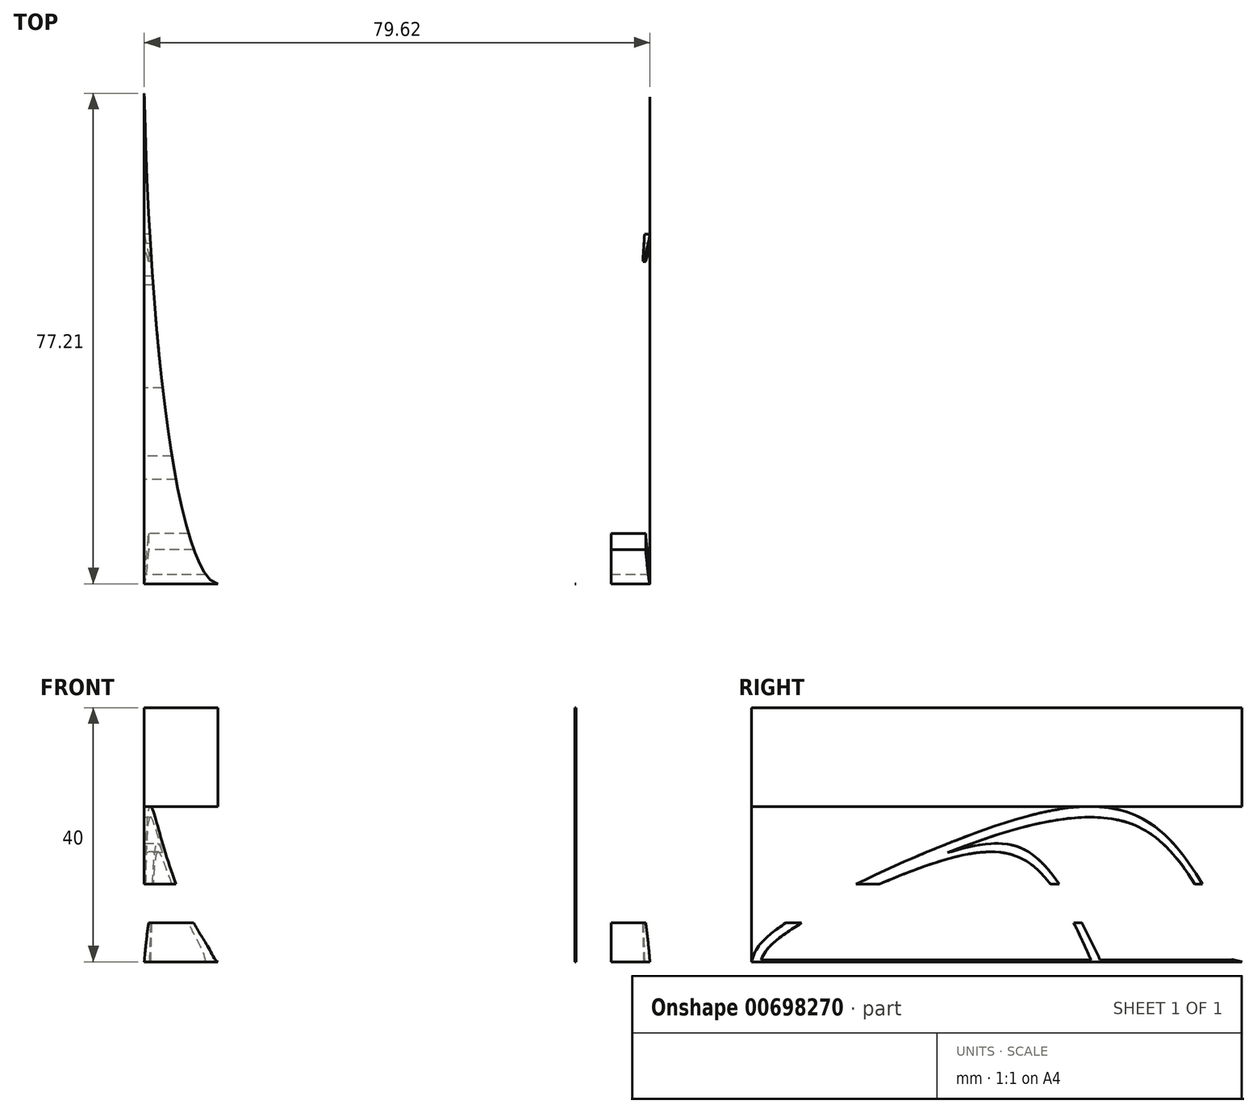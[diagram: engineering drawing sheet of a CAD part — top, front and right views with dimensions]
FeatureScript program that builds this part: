
annotation { "Feature Type Name" : "Feature", "Feature Type Description" : "" }
export const myFeature = defineFeature(function(context is Context, id is Id, definition is map)
    precondition{}
    {
        {
            var Q0;
            Q0=qCreatedBy(makeId("Top.planeOp"),FACE);
            var sketch = newSketch(context, id + "F0", { "sketchPlane" : qUnion([Q0])});
            skPoint(sketch, "E0", {"position": v(39.81, 38.84) * mm});
            skPoint(sketch, "E1", {"position": v(-39.81, 38.84) * mm});
            skPoint(sketch, "E2", {"position": v(-28, -38.37) * mm});
            skPoint(sketch, "E3", {"position": v(28, -38.37) * mm});
            skLineSegment(sketch, "E4", {"start": v(39.81, 38.84) * mm, "end": v(-39.81, 38.84) * mm});
            skLineSegment(sketch, "E5", {"start": v(28, -38.37) * mm, "end": v(-28, -38.37) * mm});
            skFitSpline(sketch, "E6.0", {"points": [v(28, -38.37) * mm, v(28.17, -38.37) * mm, v(28.4, -38.33) * mm, v(28.71, -38.2) * mm, v(29, -38.06) * mm, v(29.33, -37.8) * mm, v(29.67, -37.47) * mm, v(29.98, -37.1) * mm, v(30.36, -36.56) * mm, v(30.77, -35.86) * mm, v(31.2, -35) * mm, v(31.71, -33.82) * mm, v(32.27, -32.3) * mm, v(32.84, -30.46) * mm, v(33.35, -28.6) * mm, v(33.8, -26.73) * mm, v(34.35, -24.23) * mm, v(34.96, -21.09) * mm, v(35.6, -17.3) * mm, v(36.16, -13.5) * mm, v(36.65, -9.68) * mm, v(37.1, -5.85) * mm, v(37.5, -2.03) * mm, v(37.86, 1.8) * mm, v(38.29, 6.9) * mm, v(38.74, 13.27) * mm, v(39.18, 20.93) * mm, v(39.52, 28.6) * mm, v(39.76, 36.25) * mm, v(39.93, 43.92) * mm, v(40.03, 54.15) * mm, v(39.96, 66.93) * mm, v(39.69, 77.17) * mm, v(39.5, 82.3) * mm]});
            skFitSpline(sketch, "E7.0", {"points": [v(-39.81, 38.84) * mm, v(-39.74, 35.53) * mm, v(-39.54, 28.9) * mm, v(-39.16, 20.6) * mm, v(-38.78, 13.98) * mm, v(-38.44, 9.02) * mm, v(-38.06, 4.06) * mm, v(-37.61, -0.88) * mm, v(-37.1, -5.82) * mm, v(-36.52, -10.75) * mm, v(-35.96, -14.85) * mm, v(-35.46, -18.12) * mm, v(-35.05, -20.56) * mm, v(-34.6, -23) * mm, v(-34.1, -25.44) * mm, v(-33.53, -27.87) * mm, v(-33, -29.88) * mm, v(-32.52, -31.48) * mm, v(-32.13, -32.68) * mm, v(-31.69, -33.87) * mm, v(-31.28, -34.83) * mm, v(-30.9, -35.6) * mm, v(-30.6, -36.15) * mm, v(-30.27, -36.69) * mm, v(-29.9, -37.2) * mm, v(-29.48, -37.68) * mm, v(-28.99, -38.08) * mm, v(-28.5, -38.31) * mm, v(-28.08, -38.38) * mm, v(-27.87, -38.37) * mm, v(-27.77, -38.35) * mm]});
            skLineSegment(sketch, "E8.bottom", {"start": v(-39.81, 38.84) * mm, "end": v(39.81, 38.84) * mm});
            skLineSegment(sketch, "E8.top", {"start": v(-39.81, -38.37) * mm, "end": v(39.81, -38.37) * mm});
            skLineSegment(sketch, "E8.left", {"start": v(-39.81, 38.84) * mm, "end": v(-39.81, -38.37) * mm});
            skLineSegment(sketch, "E8.right", {"start": v(39.81, 38.84) * mm, "end": v(39.81, -38.37) * mm});
            skSolve(sketch);
        }
        {
            var Q0;
            {var subQ0=sQuery(id+"F0.wireOp",EDGE,"E6.0");Q0=makeQuery(id+"F0.imprint","IMPRINT",FACE,{"disambiguationData":[TD([[makeQuery(id+"F0.imprint","IMPRINT",EDGE,{"derivedFrom":subQ0}),-1.0]])]});}
            var Q1;
            {var subQ1=sQuery(id+"F0.wireOp",EDGE,"E6.0");Q1=makeQuery(id+"F0.imprint","IMPRINT",FACE,{"disambiguationData":[TD([[makeQuery(id+"F0.imprint","IMPRINT",EDGE,{"derivedFrom":subQ1}),1.0]])]});}
            var Q2;
            {var subQ0=sQuery(id+"F0.wireOp",EDGE,"E7.0");Q2=makeQuery(id+"F0.imprint","IMPRINT",FACE,{"disambiguationData":[TD([[makeQuery(id+"F0.imprint","IMPRINT",EDGE,{"derivedFrom":subQ0}),-1.0]])]});}
            extrude(context, id + "F1", {"entities" : qUnion([Q0, Q1, Q2]), "depth" : 40 * mm, "offsetDistance" : 25 * mm});
        }
        {
            var Q0;
            Q0=makeQuery(id+"F1.opExtrude","SWEPT_FACE",FACE,{"disambiguationData":[OSD([sQuery(id+"F0.wireOp",EDGE,"E8.left")])]});
            var sketch = newSketch(context, id + "F2", { "sketchPlane" : qUnion([Q0])});
            skFitSpline(sketch, "E9", {"points": [v(38.37, 0) * mm, v(36.2, 3.66) * mm, v(4, 19.95) * mm, v(-23.03, 22.6) * mm, v(-38.84, 0) * mm], "startDerivative": vector(-8.4, 29.66) * mm, "endDerivative": vector(-47.28, -100.41) * mm});
            skFitSpline(sketch, "E10", {"points": [v(-37.4, 0) * mm, v(-32.94, 9.49) * mm, v(-22.46, 21.28) * mm, v(4, 18.51) * mm, v(34.92, 3) * mm, v(36.93, 0) * mm], "startDerivative": vector(24.06, 55.07) * mm, "endDerivative": vector(8.6, -27.87) * mm});
            skFitSpline(sketch, "E11", {"points": [v(7.54, 17.17) * mm, v(-4.5, 17.7) * mm, v(-16.65, 0) * mm], "startDerivative": vector(-29.57, 8.19) * mm, "endDerivative": vector(-19.28, -40.17) * mm});
            skFitSpline(sketch, "E12", {"points": [v(-15.2, 0) * mm, v(-11.54, 7.65) * mm, v(-3.89, 16.4) * mm, v(8.95, 15.76) * mm, v(23.48, 10) * mm], "startDerivative": vector(15.52, 34.53) * mm, "endDerivative": vector(48.48, -20.3) * mm});
            skLineSegment(sketch, "E13", {"start": v(-38.84, 24.44) * mm, "end": v(38.37, 24.44) * mm});
            skLineSegment(sketch, "E14", {"start": v(38.06, 24.44) * mm, "end": v(-38.84, 24.44) * mm});
            skLineSegment(sketch, "E15", {"start": v(-38.84, 24.44) * mm, "end": v(-38.84, 0) * mm});
            skFitSpline(sketch, "E16", {"points": [v(38.37, 0) * mm, v(36.2, 3.66) * mm, v(4, 19.95) * mm, v(-23.03, 22.6) * mm, v(-38.84, 0) * mm], "startDerivative": vector(-8.4, 29.66) * mm, "endDerivative": vector(-47.28, -100.41) * mm});
            skLineSegment(sketch, "E17.top", {"start": v(38.06, 40) * mm, "end": v(38.37, 40) * mm});
            skLineSegment(sketch, "E17.right", {"start": v(38.37, 1.1) * mm, "end": v(38.37, 40) * mm});
            skSolve(sketch);
        }
        {
            var Q0;
            Q0=makeQuery(id+"F1.opExtrude","SWEPT_FACE",FACE,{"disambiguationData":[OSD([sQuery(id+"F0.wireOp",EDGE,"E8.top")])]});
            var sketch = newSketch(context, id + "F3", { "sketchPlane" : qUnion([Q0])});
            skPoint(sketch, "E18", {"position": v(-39.81, 24.44) * mm});
            skLineSegment(sketch, "E19", {"start": v(-39.81, 24.44) * mm, "end": v(39.81, 24.44) * mm});
            skLineSegment(sketch, "E20", {"start": v(-39.81, 24.44) * mm, "end": v(-39.81, 0) * mm});
            skPoint(sketch, "E21", {"position": v(-39.81, 12.22) * mm});
            skLineSegment(sketch, "E22", {"start": v(-39.81, 12.22) * mm, "end": v(-39.81, 0) * mm});
            skLineSegment(sketch, "E23", {"start": v(-39.81, 24.44) * mm, "end": v(-39.81, 12.22) * mm});
            skPoint(sketch, "E24", {"position": v(-39.81, 18.33) * mm});
            skPoint(sketch, "E25", {"position": v(-39.81, 6.11) * mm});
            skLineSegment(sketch, "E26", {"start": v(-39.81, 18.33) * mm, "end": v(39.81, 18.33) * mm});
            skLineSegment(sketch, "E27", {"start": v(39.81, 18.33) * mm, "end": v(39.81, 6.11) * mm});
            skLineSegment(sketch, "E28", {"start": v(39.81, 6.11) * mm, "end": v(-39.81, 6.11) * mm});
            skLineSegment(sketch, "E29", {"start": v(-39.81, 12.22) * mm, "end": v(39.81, 12.22) * mm});
            skPoint(sketch, "E30", {"position": v(-33.7, 0) * mm});
            skPoint(sketch, "E31", {"position": v(33.7, 0) * mm});
            skLineSegment(sketch, "E32", {"start": v(-33.7, 0) * mm, "end": v(-33.7, 24.44) * mm});
            skLineSegment(sketch, "E33", {"start": v(-33.7, 24.44) * mm, "end": v(33.7, 24.44) * mm});
            skLineSegment(sketch, "E34", {"start": v(33.7, 24.44) * mm, "end": v(33.7, 0) * mm});
            skFitSpline(sketch, "E35", {"points": [v(-39.81, 0) * mm, v(-33.7, 18.33) * mm, v(0, 24.44) * mm, v(33.7, 18.33) * mm, v(39.81, 0) * mm], "startDerivative": vector(9.29, 98.82) * mm, "endDerivative": vector(9.29, -98.82) * mm});
            skPoint(sketch, "E36", {"position": v(-3, 24.43) * mm});
            skPoint(sketch, "E37", {"position": v(3, 24.43) * mm});
            skPoint(sketch, "E38", {"position": v(36.81, 0) * mm});
            skPoint(sketch, "E39", {"position": v(-36.81, 0) * mm});
            skPoint(sketch, "E40", {"position": v(-34.68, 12.22) * mm});
            skPoint(sketch, "E41", {"position": v(-30.7, 18.33) * mm});
            skPoint(sketch, "E42", {"position": v(-36.13, 6.11) * mm});
            skPoint(sketch, "E43", {"position": v(-3, 21.43) * mm});
            skPoint(sketch, "E44", {"position": v(3, 21.43) * mm});
            skPoint(sketch, "E45", {"position": v(30.7, 18.33) * mm});
            skPoint(sketch, "E46", {"position": v(34.69, 12.22) * mm});
            skPoint(sketch, "E47", {"position": v(36.13, 6.11) * mm});
            skPoint(sketch, "E48", {"position": v(-39.13, 6.11) * mm});
            skPoint(sketch, "E49", {"position": v(-37.68, 12.22) * mm});
            skLineSegment(sketch, "E50", {"start": v(-3, 24.43) * mm, "end": v(-3, 0) * mm});
            skLineSegment(sketch, "E51", {"start": v(3, 24.43) * mm, "end": v(3, 0) * mm});
            skPoint(sketch, "E52", {"position": v(39.13, 6.11) * mm});
            skPoint(sketch, "E53", {"position": v(37.69, 12.22) * mm});
            skFitSpline(sketch, "E54", {"points": [v(-36.81, 0) * mm, v(-36.13, 6.1) * mm, v(-34.68, 12.22) * mm, v(-30.7, 18.33) * mm, v(-3, 21.43) * mm, v(3, 21.43) * mm, v(30.7, 18.33) * mm, v(34.69, 12.22) * mm, v(36.13, 6.1) * mm, v(36.81, 0) * mm], "startDerivative": vector(5.43, 70.33) * mm, "endDerivative": vector(5.43, -70.33) * mm});
            skSolve(sketch);
        }
        {
            var Q0;
            {var subQ0=sQuery(id+"F3.wireOp",EDGE,"E23");var subQ5=sQuery(id+"F3.wireOp",EDGE,"E26");var subQ6=makeQuery(id+"F3.imprint","INTERSECT",VERTEX,{"derivedFrom":[subQ0,subQ5]});Q0=makeQuery(id+"F3.imprint","IMPRINT",FACE,{"disambiguationData":[TD([[makeQuery(id+"F3.imprint","IMPRINT",EDGE,{"disambiguationData":[TD([[subQ6,-1.0]])],"derivedFrom":subQ5}),1.0]])]});}
            var Q1;
            {var subQ1=sQuery(id+"F3.wireOp",EDGE,"E23");var subQ3=sQuery(id+"F3.wireOp",EDGE,"E26");var subQ4=makeQuery(id+"F3.imprint","INTERSECT",VERTEX,{"derivedFrom":[subQ1,subQ3]});Q1=makeQuery(id+"F3.imprint","IMPRINT",FACE,{"disambiguationData":[TD([[makeQuery(id+"F3.imprint","IMPRINT",EDGE,{"disambiguationData":[TD([[subQ4,-1.0]])],"derivedFrom":subQ1}),1.0]])]});}
            var Q2;
            {var subQ1=sQuery(id+"F3.wireOp",EDGE,"E22");var subQ3=sQuery(id+"F3.wireOp",EDGE,"E28");var subQ4=makeQuery(id+"F3.imprint","INTERSECT",VERTEX,{"derivedFrom":[subQ1,subQ3]});Q2=makeQuery(id+"F3.imprint","IMPRINT",FACE,{"disambiguationData":[TD([[makeQuery(id+"F3.imprint","IMPRINT",EDGE,{"disambiguationData":[TD([[subQ4,1.0]])],"derivedFrom":subQ3}),-1.0]])]});}
            var Q3;
            {var subQ1=sQuery(id+"F3.wireOp",EDGE,"E22");var subQ3=sQuery(id+"F3.wireOp",EDGE,"E28");var subQ4=makeQuery(id+"F3.imprint","INTERSECT",VERTEX,{"derivedFrom":[subQ1,subQ3]});Q3=makeQuery(id+"F3.imprint","IMPRINT",FACE,{"disambiguationData":[TD([[makeQuery(id+"F3.imprint","IMPRINT",EDGE,{"disambiguationData":[TD([[subQ4,1.0]])],"derivedFrom":subQ3}),1.0]])]});}
            var Q4;
            {var subQ0=sQuery(id+"F3.wireOp",EDGE,"E28");var subQ4=sQuery(id+"F3.wireOp",EDGE,"E35");var subQ5=makeQuery(id+"F3.imprint","INTERSECT",VERTEX,{"disambiguationData":[OD(0.0)],"derivedFrom":[subQ0,subQ4]});Q4=makeQuery(id+"F3.imprint","IMPRINT",FACE,{"disambiguationData":[TD([[makeQuery(id+"F3.imprint","IMPRINT",EDGE,{"disambiguationData":[TD([[subQ5,1.0]])],"derivedFrom":subQ0}),1.0]])]});}
            var Q5;
            {var subQ1=sQuery(id+"F3.wireOp",EDGE,"E27");var subQ3=sQuery(id+"F3.wireOp",EDGE,"E29");var subQ4=makeQuery(id+"F3.imprint","INTERSECT",VERTEX,{"derivedFrom":[subQ1,subQ3]});Q5=makeQuery(id+"F3.imprint","IMPRINT",FACE,{"disambiguationData":[TD([[makeQuery(id+"F3.imprint","IMPRINT",EDGE,{"disambiguationData":[TD([[subQ4,1.0]])],"derivedFrom":subQ3}),-1.0]])]});}
            var Q6;
            {var subQ0=sQuery(id+"F3.wireOp",EDGE,"E27");var subQ5=sQuery(id+"F3.wireOp",EDGE,"E29");var subQ6=makeQuery(id+"F3.imprint","INTERSECT",VERTEX,{"derivedFrom":[subQ0,subQ5]});Q6=makeQuery(id+"F3.imprint","IMPRINT",FACE,{"disambiguationData":[TD([[makeQuery(id+"F3.imprint","IMPRINT",EDGE,{"disambiguationData":[TD([[subQ6,1.0]])],"derivedFrom":subQ5}),1.0]])]});}
            var Q7;
            {var subQ0=sQuery(id+"F3.wireOp",EDGE,"E19");var subQ1=makeQuery(id+"F1.opExtrude","SWEPT_EDGE",EDGE,{"disambiguationData":[OSD([sQuery(id+"F0.wireOp",EDGE,"E8.top"),sQuery(id+"F0.wireOp",EDGE,"E8.right")])]});var subQ2=makeQuery(id+"F3.imprint","INTERSECT",VERTEX,{"derivedFrom":[subQ1,subQ0]});Q7=makeQuery(id+"F3.imprint","IMPRINT",FACE,{"disambiguationData":[TD([[makeQuery(id+"F3.imprint","IMPRINT",EDGE,{"disambiguationData":[TD([[subQ2,1.0]])],"derivedFrom":subQ0}),-1.0]])]});}
            var Q8;
            {var subQ1=sQuery(id+"F3.wireOp",EDGE,"E33");var subQ3=sQuery(id+"F3.wireOp",EDGE,"E35");var subQ4=makeQuery(id+"F3.imprint","INTERSECT",VERTEX,{"derivedFrom":[subQ1,subQ3]});Q8=makeQuery(id+"F3.imprint","IMPRINT",FACE,{"disambiguationData":[TD([[makeQuery(id+"F3.imprint","IMPRINT",EDGE,{"disambiguationData":[TD([[subQ4,-1.0]])],"derivedFrom":subQ1}),-1.0]])]});}
            var Q9;
            {var subQ0=sQuery(id+"F3.wireOp",EDGE,"E33");var subQ3=sQuery(id+"F3.wireOp",EDGE,"E35");var subQ5=makeQuery(id+"F3.imprint","INTERSECT",VERTEX,{"derivedFrom":[subQ0,subQ3]});Q9=makeQuery(id+"F3.imprint","IMPRINT",FACE,{"disambiguationData":[TD([[makeQuery(id+"F3.imprint","IMPRINT",EDGE,{"disambiguationData":[TD([[subQ5,1.0]])],"derivedFrom":subQ0}),-1.0]])]});}
            var Q10;
            {var subQ4=sQuery(id+"F0.wireOp",EDGE,"E8.top");var subQ10=makeQuery(id+"F1.opExtrude","CAP_EDGE",EDGE,{"disambiguationData":[OSD([subQ4])],"isStart":false});Q10=makeQuery(id+"F3.imprint","IMPRINT",FACE,{"disambiguationData":[TD([[makeQuery(id+"F3.imprint","IMPRINT",EDGE,{"derivedFrom":subQ10}),-1.0]])]});}
            extrude(context, id + "F4", {"entities" : qUnion([Q0, Q1, Q2, Q3, Q4, Q5, Q6, Q7, Q8, Q9, Q10]), "operationType" : NewBodyOperationType.REMOVE, "oppositeDirection" : true, "depth" : 88.6 * mm, "offsetDistance" : 25 * mm});
        }
        {
            var Q0;
            {var subQ0=sQuery(id+"F3.wireOp",EDGE,"E54");var subQ1=sQuery(id+"F3.wireOp",EDGE,"E26");var subQ2=makeQuery(id+"F3.imprint","INTERSECT",VERTEX,{"disambiguationData":[OD(0.0)],"derivedFrom":[subQ1,subQ0]});Q0=makeQuery(id+"F3.imprint","IMPRINT",FACE,{"disambiguationData":[TD([[makeQuery(id+"F3.imprint","IMPRINT",EDGE,{"disambiguationData":[TD([[subQ2,-1.0]])],"derivedFrom":subQ1}),1.0]])]});}
            var Q1;
            {var subQ3=sQuery(id+"F3.wireOp",EDGE,"E54");var subQ6=sQuery(id+"F3.wireOp",EDGE,"E26");var subQ9=makeQuery(id+"F3.imprint","INTERSECT",VERTEX,{"disambiguationData":[OD(0.0)],"derivedFrom":[subQ6,subQ3]});Q1=makeQuery(id+"F3.imprint","IMPRINT",FACE,{"disambiguationData":[TD([[makeQuery(id+"F3.imprint","IMPRINT",EDGE,{"disambiguationData":[TD([[subQ9,-1.0]])],"derivedFrom":subQ6}),-1.0]])]});}
            var Q2;
            {var subQ0=sQuery(id+"F3.wireOp",EDGE,"E50");var subQ1=sQuery(id+"F3.wireOp",EDGE,"E28");var subQ2=makeQuery(id+"F3.imprint","INTERSECT",VERTEX,{"derivedFrom":[subQ1,subQ0]});Q2=makeQuery(id+"F3.imprint","IMPRINT",FACE,{"disambiguationData":[TD([[makeQuery(id+"F3.imprint","IMPRINT",EDGE,{"disambiguationData":[TD([[subQ2,-1.0]])],"derivedFrom":subQ1}),-1.0]])]});}
            var Q3;
            {var subQ0=sQuery(id+"F3.wireOp",EDGE,"E54");var subQ1=sQuery(id+"F3.wireOp",EDGE,"E29");var subQ2=makeQuery(id+"F3.imprint","INTERSECT",VERTEX,{"disambiguationData":[OD(0.0)],"derivedFrom":[subQ1,subQ0]});Q3=makeQuery(id+"F3.imprint","IMPRINT",FACE,{"disambiguationData":[TD([[makeQuery(id+"F3.imprint","IMPRINT",EDGE,{"disambiguationData":[TD([[subQ2,-1.0]])],"derivedFrom":subQ1}),1.0]])]});}
            var Q4;
            {var subQ0=sQuery(id+"F3.wireOp",EDGE,"E32");var subQ1=sQuery(id+"F3.wireOp",EDGE,"E28");var subQ2=makeQuery(id+"F3.imprint","INTERSECT",VERTEX,{"derivedFrom":[subQ1,subQ0]});Q4=makeQuery(id+"F3.imprint","IMPRINT",FACE,{"disambiguationData":[TD([[makeQuery(id+"F3.imprint","IMPRINT",EDGE,{"disambiguationData":[TD([[subQ2,-1.0]])],"derivedFrom":subQ1}),-1.0]])]});}
            var Q5;
            {var subQ0=sQuery(id+"F3.wireOp",EDGE,"E32");var subQ1=sQuery(id+"F3.wireOp",EDGE,"E28");var subQ2=makeQuery(id+"F3.imprint","INTERSECT",VERTEX,{"derivedFrom":[subQ1,subQ0]});Q5=makeQuery(id+"F3.imprint","IMPRINT",FACE,{"disambiguationData":[TD([[makeQuery(id+"F3.imprint","IMPRINT",EDGE,{"disambiguationData":[TD([[subQ2,-1.0]])],"derivedFrom":subQ1}),1.0]])]});}
            var Q6;
            {var subQ0=sQuery(id+"F3.wireOp",EDGE,"E50");var subQ1=sQuery(id+"F3.wireOp",EDGE,"E28");var subQ2=makeQuery(id+"F3.imprint","INTERSECT",VERTEX,{"derivedFrom":[subQ1,subQ0]});Q6=makeQuery(id+"F3.imprint","IMPRINT",FACE,{"disambiguationData":[TD([[makeQuery(id+"F3.imprint","IMPRINT",EDGE,{"disambiguationData":[TD([[subQ2,-1.0]])],"derivedFrom":subQ1}),1.0]])]});}
            var Q7;
            {var subQ0=sQuery(id+"F3.wireOp",EDGE,"E34");var subQ1=sQuery(id+"F3.wireOp",EDGE,"E28");var subQ2=makeQuery(id+"F3.imprint","INTERSECT",VERTEX,{"derivedFrom":[subQ1,subQ0]});Q7=makeQuery(id+"F3.imprint","IMPRINT",FACE,{"disambiguationData":[TD([[makeQuery(id+"F3.imprint","IMPRINT",EDGE,{"disambiguationData":[TD([[subQ2,-1.0]])],"derivedFrom":subQ1}),-1.0]])]});}
            var Q8;
            {var subQ0=sQuery(id+"F3.wireOp",EDGE,"E34");var subQ1=sQuery(id+"F3.wireOp",EDGE,"E28");var subQ2=makeQuery(id+"F3.imprint","INTERSECT",VERTEX,{"derivedFrom":[subQ1,subQ0]});Q8=makeQuery(id+"F3.imprint","IMPRINT",FACE,{"disambiguationData":[TD([[makeQuery(id+"F3.imprint","IMPRINT",EDGE,{"disambiguationData":[TD([[subQ2,-1.0]])],"derivedFrom":subQ1}),1.0]])]});}
            var Q9;
            {var subQ0=sQuery(id+"F3.wireOp",EDGE,"E51");var subQ1=sQuery(id+"F3.wireOp",EDGE,"E28");var subQ2=makeQuery(id+"F3.imprint","INTERSECT",VERTEX,{"derivedFrom":[subQ1,subQ0]});Q9=makeQuery(id+"F3.imprint","IMPRINT",FACE,{"disambiguationData":[TD([[makeQuery(id+"F3.imprint","IMPRINT",EDGE,{"disambiguationData":[TD([[subQ2,-1.0]])],"derivedFrom":subQ1}),1.0]])]});}
            var Q10;
            {var subQ0=sQuery(id+"F3.wireOp",EDGE,"E51");var subQ1=sQuery(id+"F3.wireOp",EDGE,"E28");var subQ2=makeQuery(id+"F3.imprint","INTERSECT",VERTEX,{"derivedFrom":[subQ1,subQ0]});Q10=makeQuery(id+"F3.imprint","IMPRINT",FACE,{"disambiguationData":[TD([[makeQuery(id+"F3.imprint","IMPRINT",EDGE,{"disambiguationData":[TD([[subQ2,-1.0]])],"derivedFrom":subQ1}),-1.0]])]});}
            var Q11;
            {var subQ0=sQuery(id+"F3.wireOp",EDGE,"E50");var subQ1=sQuery(id+"F3.wireOp",EDGE,"E26");var subQ2=makeQuery(id+"F3.imprint","INTERSECT",VERTEX,{"derivedFrom":[subQ1,subQ0]});Q11=makeQuery(id+"F3.imprint","IMPRINT",FACE,{"disambiguationData":[TD([[makeQuery(id+"F3.imprint","IMPRINT",EDGE,{"disambiguationData":[TD([[subQ2,-1.0]])],"derivedFrom":subQ1}),-1.0]])]});}
            var Q12;
            {var subQ0=sQuery(id+"F3.wireOp",EDGE,"E50");var subQ1=sQuery(id+"F3.wireOp",EDGE,"E26");var subQ2=makeQuery(id+"F3.imprint","INTERSECT",VERTEX,{"derivedFrom":[subQ1,subQ0]});Q12=makeQuery(id+"F3.imprint","IMPRINT",FACE,{"disambiguationData":[TD([[makeQuery(id+"F3.imprint","IMPRINT",EDGE,{"disambiguationData":[TD([[subQ2,-1.0]])],"derivedFrom":subQ1}),1.0]])]});}
            var Q13;
            {var subQ0=sQuery(id+"F3.wireOp",EDGE,"E51");var subQ1=sQuery(id+"F3.wireOp",EDGE,"E26");var subQ2=makeQuery(id+"F3.imprint","INTERSECT",VERTEX,{"derivedFrom":[subQ1,subQ0]});Q13=makeQuery(id+"F3.imprint","IMPRINT",FACE,{"disambiguationData":[TD([[makeQuery(id+"F3.imprint","IMPRINT",EDGE,{"disambiguationData":[TD([[subQ2,-1.0]])],"derivedFrom":subQ1}),1.0]])]});}
            var Q14;
            {var subQ0=sQuery(id+"F3.wireOp",EDGE,"E51");var subQ1=sQuery(id+"F3.wireOp",EDGE,"E26");var subQ2=makeQuery(id+"F3.imprint","INTERSECT",VERTEX,{"derivedFrom":[subQ1,subQ0]});Q14=makeQuery(id+"F3.imprint","IMPRINT",FACE,{"disambiguationData":[TD([[makeQuery(id+"F3.imprint","IMPRINT",EDGE,{"disambiguationData":[TD([[subQ2,-1.0]])],"derivedFrom":subQ1}),-1.0]])]});}
            var Q15;
            {var subQ0=sQuery(id+"F3.wireOp",EDGE,"E54");var subQ1=sQuery(id+"F3.wireOp",EDGE,"E28");var subQ2=makeQuery(id+"F3.imprint","INTERSECT",VERTEX,{"disambiguationData":[OD(0.0)],"derivedFrom":[subQ1,subQ0]});Q15=makeQuery(id+"F3.imprint","IMPRINT",FACE,{"disambiguationData":[TD([[makeQuery(id+"F3.imprint","IMPRINT",EDGE,{"disambiguationData":[TD([[subQ2,-1.0]])],"derivedFrom":subQ1}),-1.0]])]});}
            var Q16;
            {var subQ0=sQuery(id+"F3.wireOp",EDGE,"E34");var subQ1=sQuery(id+"F3.wireOp",EDGE,"E29");var subQ2=makeQuery(id+"F3.imprint","INTERSECT",VERTEX,{"derivedFrom":[subQ1,subQ0]});Q16=makeQuery(id+"F3.imprint","IMPRINT",FACE,{"disambiguationData":[TD([[makeQuery(id+"F3.imprint","IMPRINT",EDGE,{"disambiguationData":[TD([[subQ2,-1.0]])],"derivedFrom":subQ1}),1.0]])]});}
            var Q17;
            {var subQ0=sQuery(id+"F3.wireOp",EDGE,"E54");var subQ1=sQuery(id+"F3.wireOp",EDGE,"E28");var subQ2=makeQuery(id+"F3.imprint","INTERSECT",VERTEX,{"disambiguationData":[OD(0.0)],"derivedFrom":[subQ1,subQ0]});Q17=makeQuery(id+"F3.imprint","IMPRINT",FACE,{"disambiguationData":[TD([[makeQuery(id+"F3.imprint","IMPRINT",EDGE,{"disambiguationData":[TD([[subQ2,-1.0]])],"derivedFrom":subQ1}),1.0]])]});}
            extrude(context, id + "F5", {"entities" : qUnion([Q0, Q1, Q2, Q3, Q4, Q5, Q6, Q7, Q8, Q9, Q10, Q11, Q12, Q13, Q14, Q15, Q16, Q17]), "operationType" : NewBodyOperationType.REMOVE, "oppositeDirection" : true, "depth" : 97.6 * mm, "offsetDistance" : 25 * mm});
        }
        {
            var Q0;
            {var subQ0=sQuery(id+"F2.wireOp",EDGE,"E15");Q0=makeQuery(id+"F2.imprint","IMPRINT",FACE,{"disambiguationData":[TD([[makeQuery(id+"F2.imprint","IMPRINT",EDGE,{"derivedFrom":subQ0}),1.0]])]});}
            var Q1;
            {var subQ3=sQuery(id+"F2.wireOp",EDGE,"E11");Q1=makeQuery(id+"F2.imprint","IMPRINT",FACE,{"disambiguationData":[TD([[makeQuery(id+"F2.imprint","IMPRINT",EDGE,{"derivedFrom":subQ3}),-1.0]])]});}
            var Q2;
            {var subQ1=sQuery(id+"F2.wireOp",EDGE,"E13");Q2=makeQuery(id+"F2.imprint","IMPRINT",FACE,{"disambiguationData":[TD([[makeQuery(id+"F2.imprint","IMPRINT",EDGE,{"derivedFrom":subQ1}),-1.0]])]});}
            var Q3;
            {var subQ3=sQuery(id+"F2.wireOp",EDGE,"E12");Q3=makeQuery(id+"F2.imprint","IMPRINT",FACE,{"disambiguationData":[TD([[makeQuery(id+"F2.imprint","IMPRINT",EDGE,{"derivedFrom":subQ3}),-1.0]])]});}
            extrude(context, id + "F6", {"entities" : qUnion([Q0, Q1, Q2, Q3]), "operationType" : NewBodyOperationType.REMOVE, "oppositeDirection" : true, "depth" : 79.6 * mm, "offsetDistance" : 25 * mm});
        }
    });
